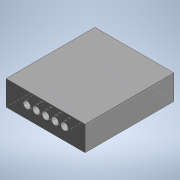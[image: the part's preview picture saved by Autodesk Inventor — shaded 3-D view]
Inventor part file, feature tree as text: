
AUTODESK INVENTOR PART (.ipt)
format: ipt  version: 2022 (Build 260153000, 153)  size: 124,416 bytes
history: native  units: mm (DEFAULTED — no unit token found)
features: sketch x2, hole x2, extrude x1
ambient origin geometry x8: Origin, YZ Plane, XZ Plane, XY Plane, X Axis, Y Axis, Z Axis, Center Point
bodies: Solid1 (feature_tree)
feature tree (5):
  sketch  "Sketch1"  dims[d0=0.0mm d1=57.15mm d2=57.15mm d3=0.0mm]
  sketch  "Sketch2"  dims[d4=4.7625mm d5=19.05mm d6=9.525mm d7=6.35mm d8=14.3117mm d9=44.499505mm d10=20.594885mm d11=4.7625mm d12=19.05mm d13=9.525mm d14=6.35mm d15=14.3117mm d16=44.499505mm d17=20.594885mm]
  extrude  "Extrusion1"  Depth=57.15mm TaperAngle=0.0deg
  hole  "Hole1"  [1 undecoded]
  hole  "Hole2"  [1 undecoded]
note: 2 required parameter values undecoded (feature->parameter linkage not recoverable at this tier; creation-order binding heuristic only, values carry confidence <= 0.55)
